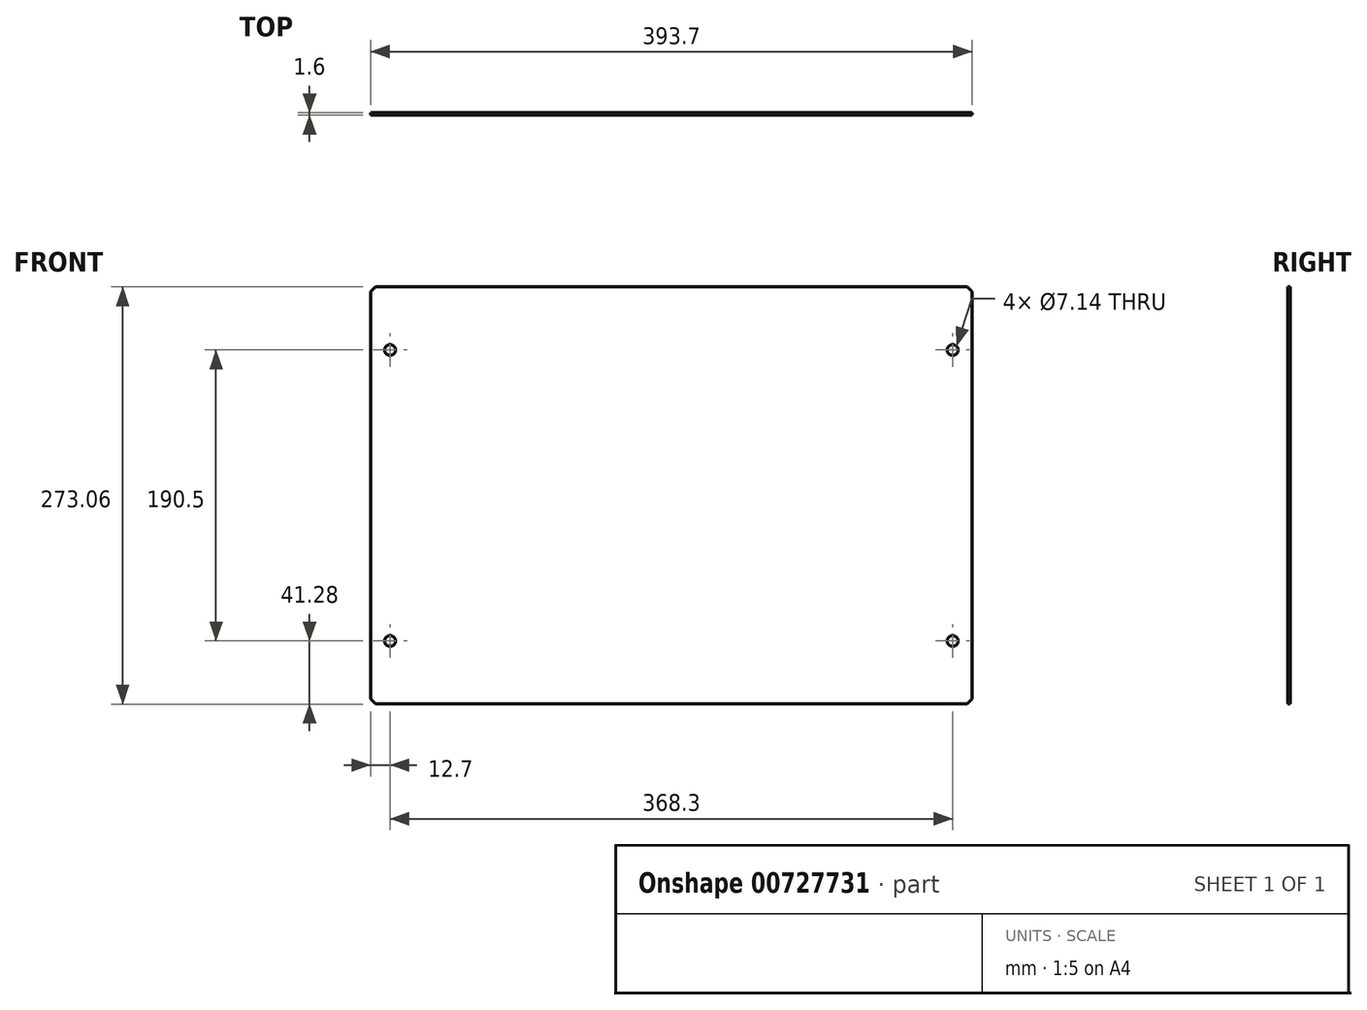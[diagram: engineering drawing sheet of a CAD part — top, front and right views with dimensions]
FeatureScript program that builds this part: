
annotation { "Feature Type Name" : "Feature", "Feature Type Description" : "" }
export const myFeature = defineFeature(function(context is Context, id is Id, definition is map)
    precondition{}
    {
        {
            var Q0;
            Q0=qCreatedBy(makeId("Front.planeOp"),FACE);
            var sketch = newSketch(context, id + "F0", { "sketchPlane" : qUnion([Q0])});
            skLineSegment(sketch, "E0.bottom", {"start": v(-196.85, 136.53) * mm, "end": v(196.85, 136.52) * mm});
            skLineSegment(sketch, "E0.top", {"start": v(-196.85, -136.52) * mm, "end": v(196.85, -136.53) * mm});
            skLineSegment(sketch, "E0.left", {"start": v(-196.85, 136.53) * mm, "end": v(-196.85, -136.53) * mm});
            skLineSegment(sketch, "E0.right", {"start": v(196.85, 136.53) * mm, "end": v(196.85, -136.53) * mm});
            skLineSegment(sketch, "E1", {"start": v(0, 136.53) * mm, "end": v(0, 0) * mm, "construction": true});
            skLineSegment(sketch, "E2", {"start": v(0, 0) * mm, "end": v(-196.85, 0) * mm, "construction": true});
            skSolve(sketch);
        }
        {
            var Q0;
            Q0 = qSketchRegion(id + "F0", true);
            extrude(context, id + "F1", {"entities" : qUnion([Q0]), "depth" : 1.6 * mm, "offsetDistance" : 25.4 * mm});
        }
        {
            var Q0;
            Q0=makeQuery(id+"F1.opExtrude","SWEPT_EDGE",EDGE,{"disambiguationData":[OSD([sQuery(id+"F0.wireOp",EDGE,"E0.bottom"),sQuery(id+"F0.wireOp",EDGE,"E0.left")])]});
            var Q1;
            Q1=makeQuery(id+"F1.opExtrude","SWEPT_EDGE",EDGE,{"disambiguationData":[OSD([sQuery(id+"F0.wireOp",EDGE,"E0.top"),sQuery(id+"F0.wireOp",EDGE,"E0.left")])]});
            var Q2;
            Q2=makeQuery(id+"F1.opExtrude","SWEPT_EDGE",EDGE,{"disambiguationData":[OSD([sQuery(id+"F0.wireOp",EDGE,"E0.top"),sQuery(id+"F0.wireOp",EDGE,"E0.right")])]});
            var Q3;
            Q3=makeQuery(id+"F1.opExtrude","SWEPT_EDGE",EDGE,{"disambiguationData":[OSD([sQuery(id+"F0.wireOp",EDGE,"E0.bottom"),sQuery(id+"F0.wireOp",EDGE,"E0.right")])]});
            chamfer(context, id + "F2", {"entities" : qUnion([Q0, Q1, Q2, Q3]), "width" : 3.17 * mm, "tangentPropagation" : true});
        }
        {
            var Q0;
            Q0=makeQuery(id+"F1.opExtrude","CAP_FACE",FACE,{"disambiguationData":[OSD([sQuery(id+"F0.wireOp",EDGE,"E0.bottom"),sQuery(id+"F0.wireOp",EDGE,"E0.top"),sQuery(id+"F0.wireOp",EDGE,"E0.left"),sQuery(id+"F0.wireOp",EDGE,"E0.right")])],"isStart":false});
            var sketch = newSketch(context, id + "F3", { "sketchPlane" : qUnion([Q0])});
            skLineSegment(sketch, "E3.bottom", {"start": v(-184.15, 95.25) * mm, "end": v(184.15, 95.25) * mm, "construction": true});
            skLineSegment(sketch, "E3.top", {"start": v(-184.15, -95.25) * mm, "end": v(184.15, -95.25) * mm, "construction": true});
            skLineSegment(sketch, "E3.left", {"start": v(-184.15, 95.25) * mm, "end": v(-184.15, -95.25) * mm, "construction": true});
            skLineSegment(sketch, "E3.right", {"start": v(184.15, 95.25) * mm, "end": v(184.15, -95.25) * mm, "construction": true});
            skLineSegment(sketch, "E4", {"start": v(0, 95.25) * mm, "end": v(0, 0) * mm, "construction": true});
            skLineSegment(sketch, "E5", {"start": v(0, 0) * mm, "end": v(-184.15, 0) * mm, "construction": true});
            skSolve(sketch);
        }
        {
            var Q0;
            Q0=sQuery(id+"F3.wireOp",VERTEX,"E3.bottom.start");
            var Q1;
            Q1=sQuery(id+"F3.wireOp",VERTEX,"E3.right.start");
            var Q2;
            Q2=sQuery(id+"F3.wireOp",VERTEX,"E3.right.end");
            var Q3;
            Q3=sQuery(id+"F3.wireOp",VERTEX,"E3.left.end");
            var Q4;
            Q4=makeQuery(id+"F1.opExtrude","SWEPT_BODY",BODY,{"disambiguationData":[OSD([sQuery(id+"F0.wireOp",EDGE,"E0.bottom"),sQuery(id+"F0.wireOp",EDGE,"E0.top"),sQuery(id+"F0.wireOp",EDGE,"E0.left"),sQuery(id+"F0.wireOp",EDGE,"E0.right")])]});
            hole(context, id + "F4", {"style" : HoleStyle.SIMPLE, "endStyle" : HoleEndStyle.THROUGH, "holeDiameter" : 7.14 * mm, "majorDiameter" : 6.35 * mm, "isTappedThrough" : true, "tappedDepth" : 12.7 * mm, "tapClearance" : 3, "locations" : qUnion([Q0, Q1, Q2, Q3]), "scope" : qUnion([Q4])});
        }
    });
